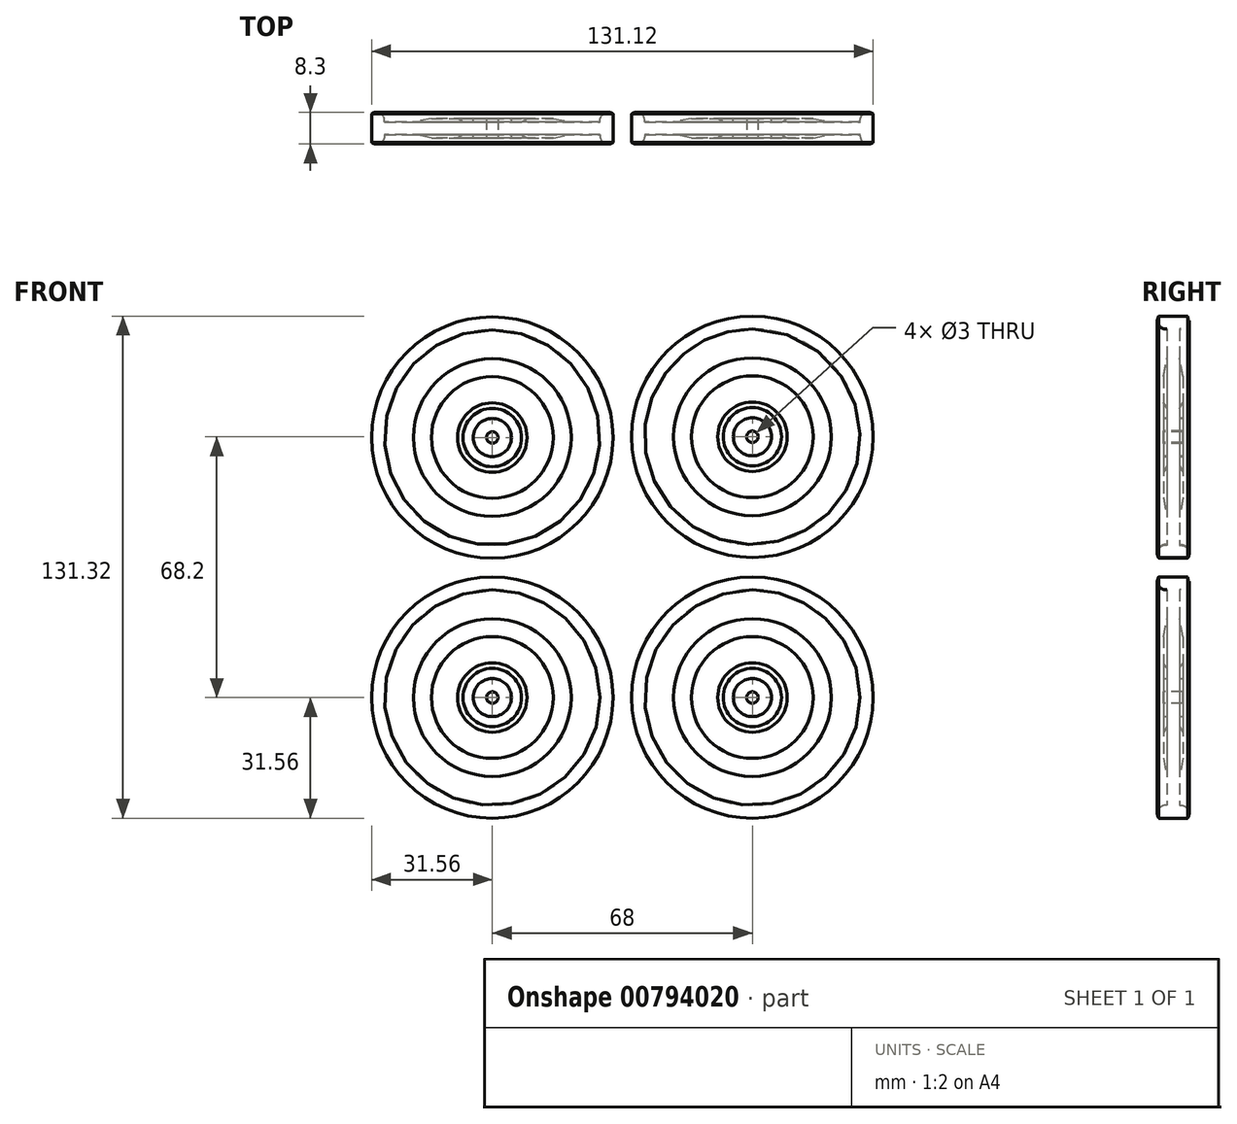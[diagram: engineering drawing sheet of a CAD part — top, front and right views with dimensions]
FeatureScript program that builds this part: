
annotation { "Feature Type Name" : "Feature", "Feature Type Description" : "" }
export const myFeature = defineFeature(function(context is Context, id is Id, definition is map)
    precondition{}
    {
        {
            var Q0;
            Q0=qCreatedBy(makeId("Right.planeOp"),FACE);
            var sketch = newSketch(context, id + "F0", { "sketchPlane" : qUnion([Q0])});
            skLineSegment(sketch, "E0", {"start": v(0, 31.56) * mm, "end": v(-3.78, 31.56) * mm});
            skArc(sketch, "E1", {"start": v(-3.78, 31.56) * mm, "mid": v(-3.8, 29.18) * mm, "end": v(-1.65, 28.19) * mm});
            skLineSegment(sketch, "E2", {"start": v(-1.65, 28.19) * mm, "end": v(-1.65, 20.62) * mm});
            skLineSegment(sketch, "E3", {"start": v(-1.65, 20.62) * mm, "end": v(-2.55, 15.92) * mm});
            skLineSegment(sketch, "E4", {"start": v(-2.55, 15.92) * mm, "end": v(-2.55, 9.08) * mm});
            skLineSegment(sketch, "E5", {"start": v(-2.55, 9.08) * mm, "end": v(-1.65, 7.63) * mm});
            skLineSegment(sketch, "E6", {"start": v(-1.65, 7.63) * mm, "end": v(-1.65, 4.99) * mm});
            skLineSegment(sketch, "E7", {"start": v(-1.65, 4.99) * mm, "end": v(-2.55, 4.99) * mm});
            skLineSegment(sketch, "E8", {"start": v(-2.55, 4.99) * mm, "end": v(-2.55, 0) * mm});
            skLineSegment(sketch, "E9", {"start": v(-2.55, 0) * mm, "end": v(0, 0) * mm});
            skLineSegment(sketch, "E10.MirrorCS", {"start": v(0, 31.56) * mm, "end": v(3.78, 31.56) * mm});
            skArc(sketch, "E11.MirrorCS", {"start": v(3.78, 31.56) * mm, "mid": v(3.8, 29.18) * mm, "end": v(1.65, 28.19) * mm});
            skLineSegment(sketch, "E12.MirrorCS", {"start": v(1.65, 28.19) * mm, "end": v(1.65, 20.62) * mm});
            skLineSegment(sketch, "E13.MirrorCS", {"start": v(1.65, 20.62) * mm, "end": v(2.55, 15.92) * mm});
            skLineSegment(sketch, "E14.MirrorCS", {"start": v(2.55, 15.92) * mm, "end": v(2.55, 9.08) * mm});
            skLineSegment(sketch, "E15.MirrorCS", {"start": v(1.65, 7.63) * mm, "end": v(1.65, 4.99) * mm});
            skLineSegment(sketch, "E16.MirrorCS", {"start": v(2.55, 9.08) * mm, "end": v(1.65, 7.63) * mm});
            skLineSegment(sketch, "E17.MirrorCS", {"start": v(1.65, 4.99) * mm, "end": v(2.55, 4.99) * mm});
            skLineSegment(sketch, "E18.MirrorCS", {"start": v(2.55, 4.99) * mm, "end": v(2.55, 0) * mm});
            skLineSegment(sketch, "E19.MirrorCS", {"start": v(2.55, 0) * mm, "end": v(0, 0) * mm});
            skSolve(sketch);
        }
        {
            var Q0;
            Q0=makeQuery(id+"F0.imprint","IMPRINT",FACE,{"disambiguationData":[TD([[makeQuery(id+"F0.imprint","IMPRINT",EDGE,{"derivedFrom":sQuery(id+"F0.wireOp",EDGE,"E0")}),1.0]])]});
            var Q1;
            Q1=sQuery(id+"F0.wireOp",EDGE,"E19.MirrorCS");
            revolve(context, id + "F1", {"surfaceOperationType" : NewSurfaceOperationType.NEW, "entities" : qUnion([Q0]), "axis" : qUnion([Q1]), "revolveType" : RevolveType.FULL});
        }
        {
            var Q0;
            Q0=qCreatedBy(makeId("Front.planeOp"),FACE);
            var sketch = newSketch(context, id + "F2", { "sketchPlane" : qUnion([Q0])});
            skCircle(sketch, "E20", {"center": v(0, 0) * mm, "radius": 1.5 * mm});
            skSolve(sketch);
        }
        {
            var Q0;
            Q0 = qSketchRegion(id + "F2", true);
            extrude(context, id + "F3", {"entities" : qUnion([Q0]), "operationType" : NewBodyOperationType.REMOVE, "oppositeDirection" : true, "depth" : 5 * mm, "offsetDistance" : 25 * mm, "hasSecondDirection" : true, "secondDirectionOppositeDirection" : false, "secondDirectionDepth" : 25 * mm});
        }
        {
            var Q0;
            Q0=makeQuery(id+"F1.opRevolve","SWEPT_BODY",BODY,{"disambiguationData":[OSD([sQuery(id+"F0.wireOp",EDGE,"E0"),sQuery(id+"F0.wireOp",EDGE,"E1"),sQuery(id+"F0.wireOp",EDGE,"E2"),sQuery(id+"F0.wireOp",EDGE,"E3"),sQuery(id+"F0.wireOp",EDGE,"E4"),sQuery(id+"F0.wireOp",EDGE,"E5"),sQuery(id+"F0.wireOp",EDGE,"E6"),sQuery(id+"F0.wireOp",EDGE,"E7"),sQuery(id+"F0.wireOp",EDGE,"E8"),sQuery(id+"F0.wireOp",EDGE,"E9"),sQuery(id+"F0.wireOp",EDGE,"E10.MirrorCS"),sQuery(id+"F0.wireOp",EDGE,"E11.MirrorCS"),sQuery(id+"F0.wireOp",EDGE,"E12.MirrorCS"),sQuery(id+"F0.wireOp",EDGE,"E13.MirrorCS"),sQuery(id+"F0.wireOp",EDGE,"E14.MirrorCS"),sQuery(id+"F0.wireOp",EDGE,"E15.MirrorCS"),sQuery(id+"F0.wireOp",EDGE,"E16.MirrorCS"),sQuery(id+"F0.wireOp",EDGE,"E17.MirrorCS"),sQuery(id+"F0.wireOp",EDGE,"E18.MirrorCS"),sQuery(id+"F0.wireOp",EDGE,"E19.MirrorCS")])]});
            transform(context, id + "F4", {"entities" : qUnion([Q0]), "transformType" : TransformType.TRANSLATION_3D, "dx" : 68 * mm, "dy" : 0 * mm, "dz" : 0 * mm, "makeCopy" : true});
        }
        {
            var Q0;
            Q0=makeQuery(id+"F1.opRevolve","SWEPT_BODY",BODY,{"disambiguationData":[OSD([sQuery(id+"F0.wireOp",EDGE,"E0"),sQuery(id+"F0.wireOp",EDGE,"E1"),sQuery(id+"F0.wireOp",EDGE,"E2"),sQuery(id+"F0.wireOp",EDGE,"E3"),sQuery(id+"F0.wireOp",EDGE,"E4"),sQuery(id+"F0.wireOp",EDGE,"E5"),sQuery(id+"F0.wireOp",EDGE,"E6"),sQuery(id+"F0.wireOp",EDGE,"E7"),sQuery(id+"F0.wireOp",EDGE,"E8"),sQuery(id+"F0.wireOp",EDGE,"E9"),sQuery(id+"F0.wireOp",EDGE,"E10.MirrorCS"),sQuery(id+"F0.wireOp",EDGE,"E11.MirrorCS"),sQuery(id+"F0.wireOp",EDGE,"E12.MirrorCS"),sQuery(id+"F0.wireOp",EDGE,"E13.MirrorCS"),sQuery(id+"F0.wireOp",EDGE,"E14.MirrorCS"),sQuery(id+"F0.wireOp",EDGE,"E15.MirrorCS"),sQuery(id+"F0.wireOp",EDGE,"E16.MirrorCS"),sQuery(id+"F0.wireOp",EDGE,"E17.MirrorCS"),sQuery(id+"F0.wireOp",EDGE,"E18.MirrorCS"),sQuery(id+"F0.wireOp",EDGE,"E19.MirrorCS")])]});
            transform(context, id + "F5", {"entities" : qUnion([Q0]), "transformType" : TransformType.TRANSLATION_3D, "dx" : 0 * mm, "dy" : 0 * mm, "dz" : 68 * mm, "makeCopy" : true});
        }
        {
            var Q0;
            Q0=makeQuery(id+"F4.opPattern","COPY",BODY,{"derivedFrom":makeQuery(id+"F1.opRevolve","SWEPT_BODY",BODY,{"disambiguationData":[OSD([sQuery(id+"F0.wireOp",EDGE,"E0"),sQuery(id+"F0.wireOp",EDGE,"E1"),sQuery(id+"F0.wireOp",EDGE,"E2"),sQuery(id+"F0.wireOp",EDGE,"E3"),sQuery(id+"F0.wireOp",EDGE,"E4"),sQuery(id+"F0.wireOp",EDGE,"E5"),sQuery(id+"F0.wireOp",EDGE,"E6"),sQuery(id+"F0.wireOp",EDGE,"E7"),sQuery(id+"F0.wireOp",EDGE,"E8"),sQuery(id+"F0.wireOp",EDGE,"E9"),sQuery(id+"F0.wireOp",EDGE,"E10.MirrorCS"),sQuery(id+"F0.wireOp",EDGE,"E11.MirrorCS"),sQuery(id+"F0.wireOp",EDGE,"E12.MirrorCS"),sQuery(id+"F0.wireOp",EDGE,"E13.MirrorCS"),sQuery(id+"F0.wireOp",EDGE,"E14.MirrorCS"),sQuery(id+"F0.wireOp",EDGE,"E15.MirrorCS"),sQuery(id+"F0.wireOp",EDGE,"E16.MirrorCS"),sQuery(id+"F0.wireOp",EDGE,"E17.MirrorCS"),sQuery(id+"F0.wireOp",EDGE,"E18.MirrorCS"),sQuery(id+"F0.wireOp",EDGE,"E19.MirrorCS")])]}),"instanceName":"1"});
            transform(context, id + "F6", {"entities" : qUnion([Q0]), "transformType" : TransformType.TRANSLATION_3D, "dx" : 0 * mm, "dy" : 0 * mm, "dz" : 68.2 * mm, "makeCopy" : true});
        }
    });
